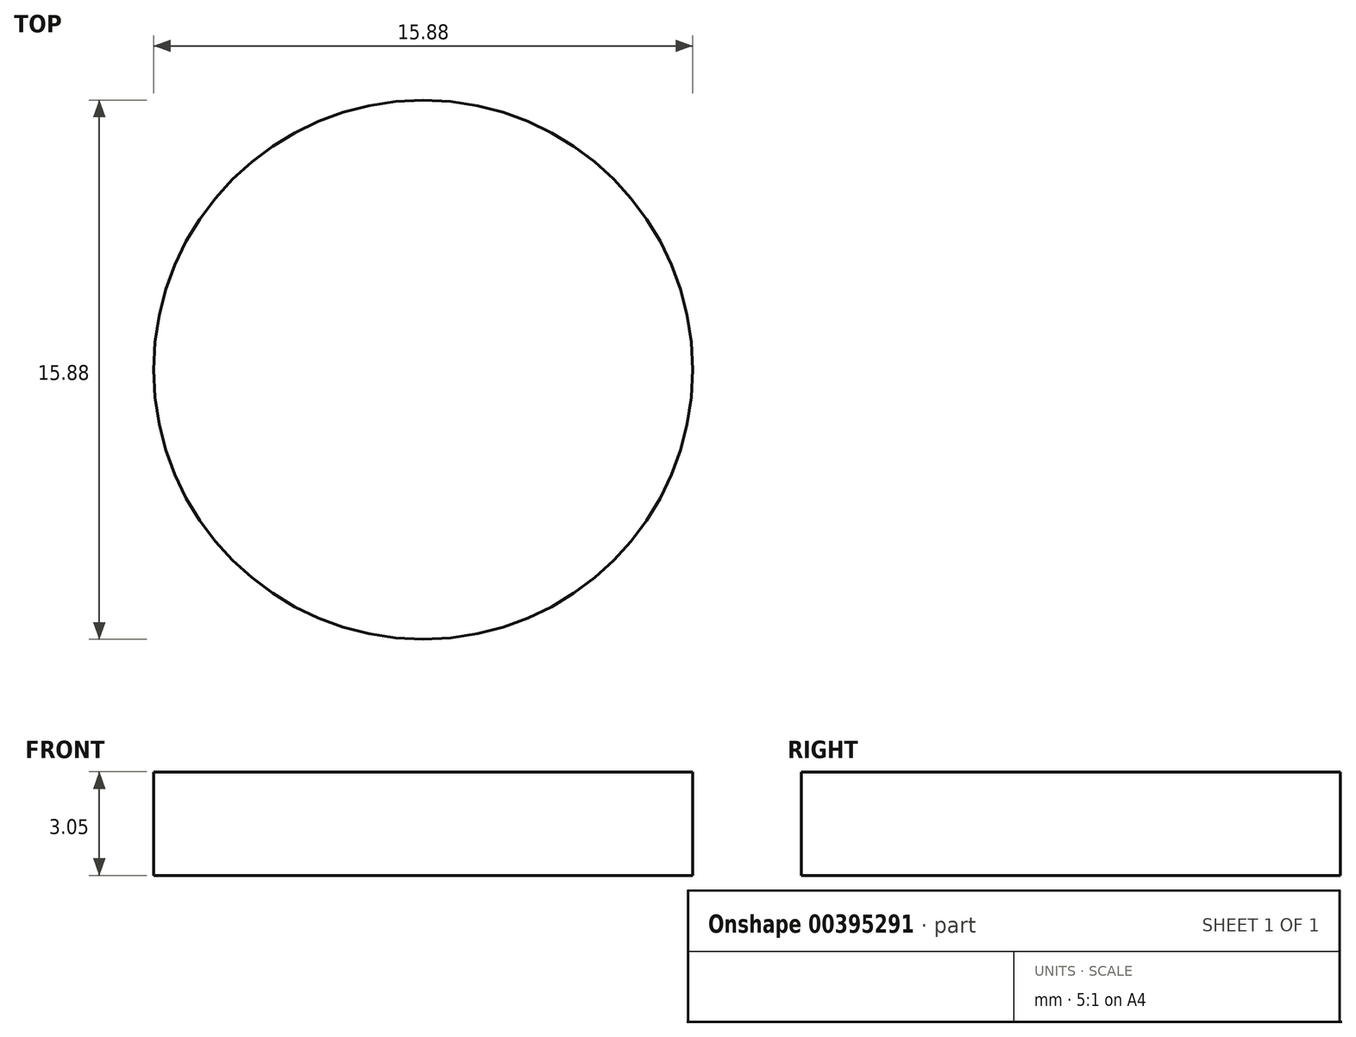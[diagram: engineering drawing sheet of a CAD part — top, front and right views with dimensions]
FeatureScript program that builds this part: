
annotation { "Feature Type Name" : "Feature", "Feature Type Description" : "" }
export const myFeature = defineFeature(function(context is Context, id is Id, definition is map)
    precondition{}
    {
        {
            var Q0;
            Q0=qCreatedBy(makeId("Top.planeOp"),FACE);
            var sketch = newSketch(context, id + "F0", { "sketchPlane" : qUnion([Q0])});
            skCircle(sketch, "E0", {"center": v(0, 0) * mm, "radius": 7.94 * mm});
            skSolve(sketch);
        }
        {
            var Q0;
            Q0=sQuery(id+"F0.wireOp",EDGE,"E0");
            extrude(context, id + "F1", {"bodyType" : ToolBodyType.SURFACE, "surfaceEntities" : qUnion([Q0]), "depth" : 3.05 * mm});
        }
    });
